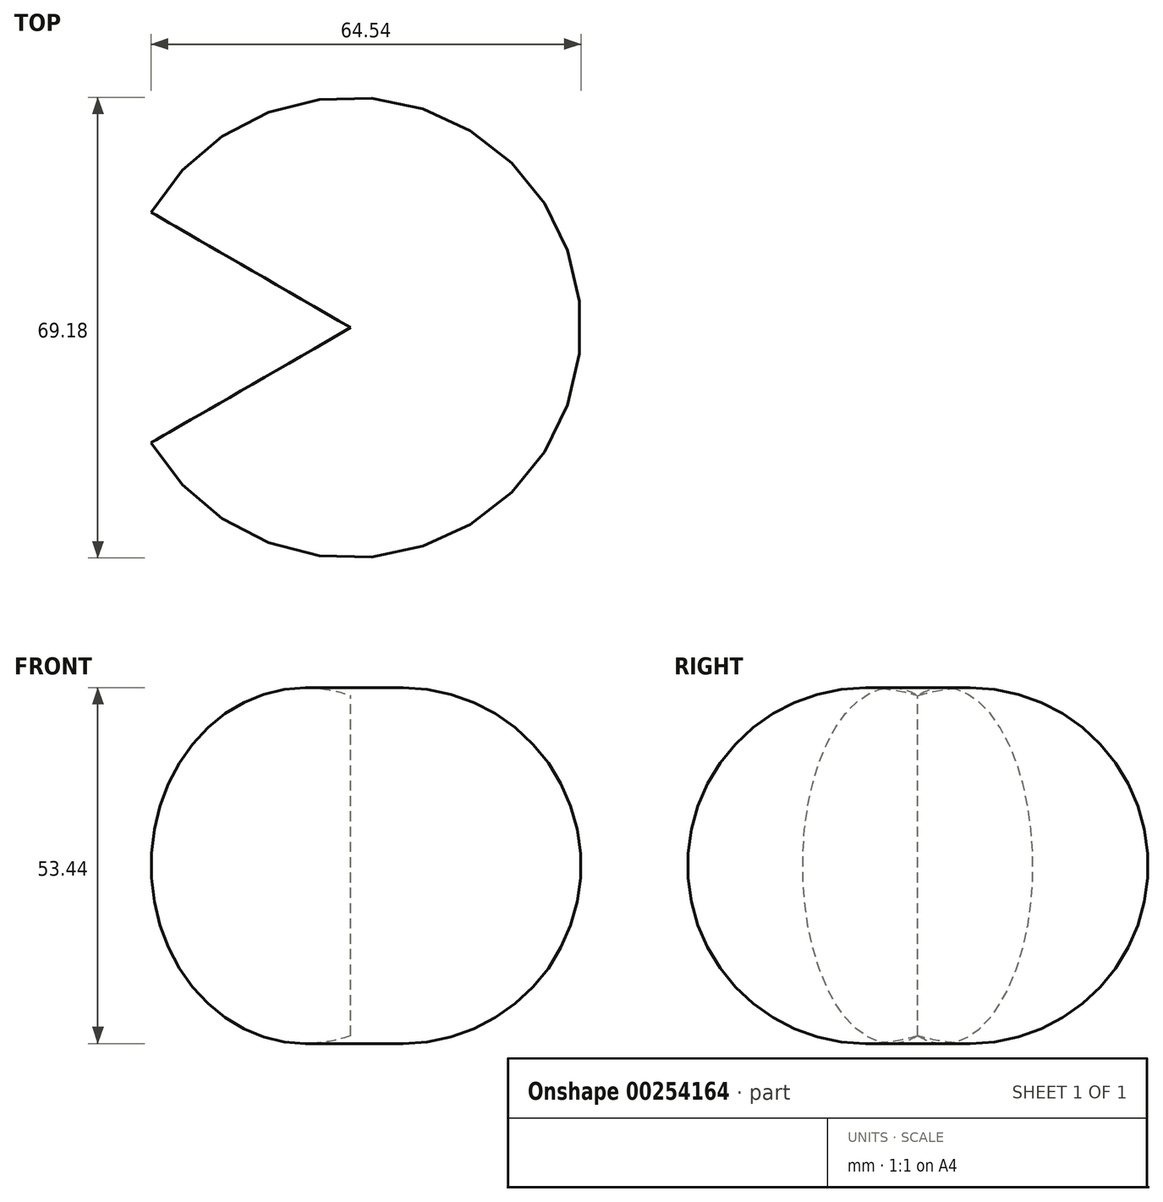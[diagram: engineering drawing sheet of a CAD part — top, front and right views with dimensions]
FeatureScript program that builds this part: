
annotation { "Feature Type Name" : "Feature", "Feature Type Description" : "" }
export const myFeature = defineFeature(function(context is Context, id is Id, definition is map)
    precondition{}
    {
        {
            var Q0;
            Q0=qCreatedBy(makeId("Front.planeOp"),FACE);
            var sketch = newSketch(context, id + "F0", { "sketchPlane" : qUnion([Q0])});
            skLineSegment(sketch, "E0", {"start": v(0, 0) * mm, "end": v(0, 51.08) * mm});
            skArc(sketch, "E1", {"start": v(0, 0) * mm, "mid": v(34.59, 25.54) * mm, "end": v(0, 51.08) * mm});
            skSolve(sketch);
        }
        {
            var Q0;
            Q0=makeQuery(id+"F0.imprint","IMPRINT",FACE,{"disambiguationData":[TD([[makeQuery(id+"F0.imprint","IMPRINT",EDGE,{"derivedFrom":sQuery(id+"F0.wireOp",EDGE,"E0")}),-1.0]])]});
            var Q1;
            Q1=sQuery(id+"F0.wireOp",EDGE,"E0");
            revolve(context, id + "F1", {"entities" : qUnion([Q0]), "axis" : qUnion([Q1]), "revolveType" : RevolveType.SYMMETRIC, "oppositeDirection" : true, "angle" : 300 * degree});
        }
    });
